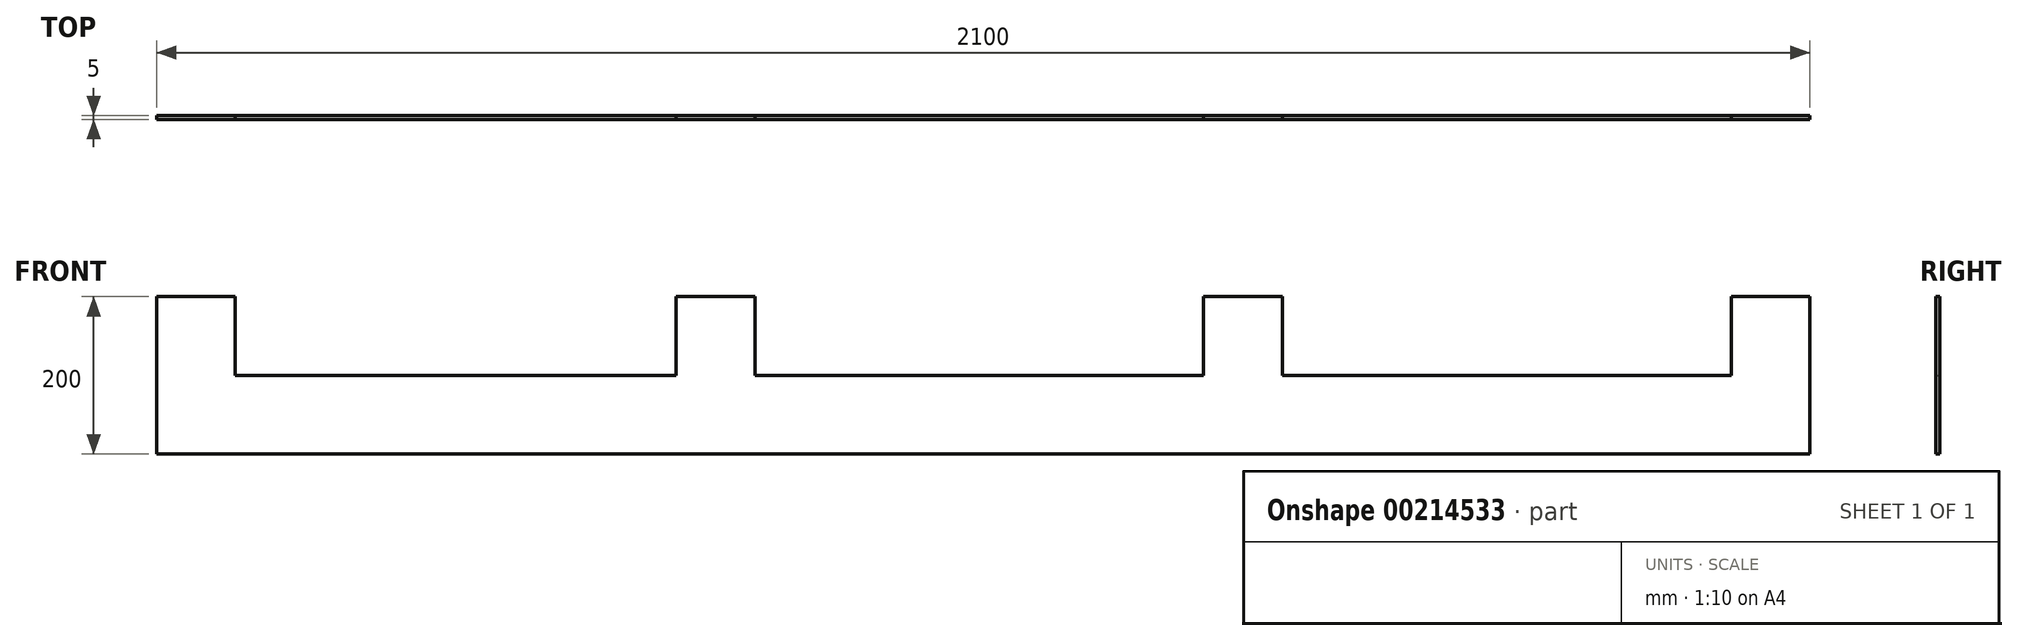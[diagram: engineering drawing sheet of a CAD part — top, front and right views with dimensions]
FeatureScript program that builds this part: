
annotation { "Feature Type Name" : "Feature", "Feature Type Description" : "" }
export const myFeature = defineFeature(function(context is Context, id is Id, definition is map)
    precondition{}
    {
        {
            var Q0;
            Q0=qCreatedBy(makeId("Front.planeOp"),FACE);
            var sketch = newSketch(context, id + "F0", { "sketchPlane" : qUnion([Q0])});
            skLineSegment(sketch, "E0", {"start": v(-1050, 0) * mm, "end": v(1050, 0) * mm});
            skLineSegment(sketch, "E1", {"start": v(1050, 0) * mm, "end": v(1050, 200) * mm});
            skLineSegment(sketch, "E2", {"start": v(1050, 200) * mm, "end": v(950, 200) * mm});
            skLineSegment(sketch, "E3", {"start": v(950, 200) * mm, "end": v(950, 100) * mm});
            skLineSegment(sketch, "E4", {"start": v(950, 100) * mm, "end": v(380, 100) * mm});
            skLineSegment(sketch, "E5", {"start": v(380, 100) * mm, "end": v(380, 200) * mm});
            skLineSegment(sketch, "E6", {"start": v(380, 200) * mm, "end": v(280, 200) * mm});
            skLineSegment(sketch, "E7", {"start": v(280, 200) * mm, "end": v(280, 100) * mm});
            skLineSegment(sketch, "E8", {"start": v(280, 100) * mm, "end": v(-290, 100) * mm});
            skLineSegment(sketch, "E9", {"start": v(-290, 100) * mm, "end": v(-290, 200) * mm});
            skLineSegment(sketch, "E10", {"start": v(-290, 200) * mm, "end": v(-390, 200) * mm});
            skLineSegment(sketch, "E11", {"start": v(-390, 200) * mm, "end": v(-390, 100) * mm});
            skLineSegment(sketch, "E12", {"start": v(-390, 100) * mm, "end": v(-950, 100) * mm});
            skLineSegment(sketch, "E13", {"start": v(-950, 100) * mm, "end": v(-950, 200) * mm});
            skLineSegment(sketch, "E14", {"start": v(-950, 200) * mm, "end": v(-1050, 200) * mm});
            skLineSegment(sketch, "E15", {"start": v(-1050, 200) * mm, "end": v(-1050, 0) * mm});
            skSolve(sketch);
        }
        {
            var Q0;
            Q0 = qSketchRegion(id + "F0", true);
            extrude(context, id + "F1", {"entities" : qUnion([Q0]), "depth" : 5 * mm});
        }
    });
